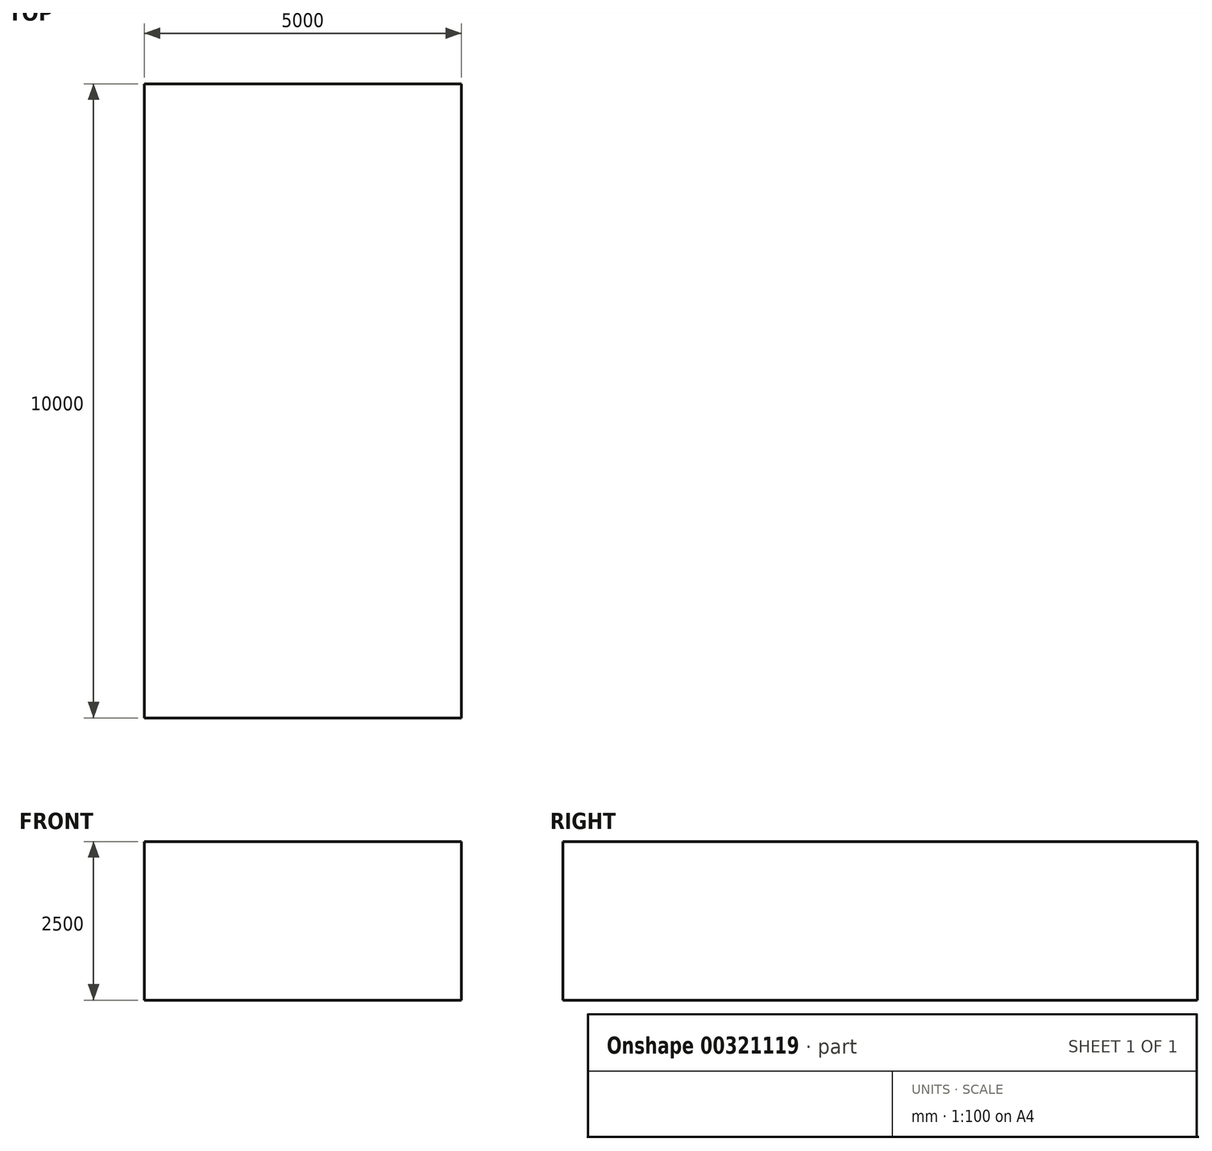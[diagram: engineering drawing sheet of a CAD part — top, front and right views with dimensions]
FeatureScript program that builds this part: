
annotation { "Feature Type Name" : "Feature", "Feature Type Description" : "" }
export const myFeature = defineFeature(function(context is Context, id is Id, definition is map)
    precondition{}
    {
        {
            var Q0;
            Q0=qCreatedBy(makeId("Front.planeOp"),FACE);
            var sketch = newSketch(context, id + "F0", { "sketchPlane" : qUnion([Q0])});
            skLineSegment(sketch, "E0.bottom", {"start": v(0, 0) * mm, "end": v(5000, 0) * mm});
            skLineSegment(sketch, "E0.top", {"start": v(0, -2500) * mm, "end": v(5000, -2500) * mm});
            skLineSegment(sketch, "E0.left", {"start": v(0, 0) * mm, "end": v(0, -2500) * mm});
            skLineSegment(sketch, "E0.right", {"start": v(5000, 0) * mm, "end": v(5000, -2500) * mm});
            skSolve(sketch);
        }
        {
            var Q0;
            Q0=makeQuery(id+"F0.imprint","IMPRINT",FACE,{"disambiguationData":[TD([[makeQuery(id+"F0.imprint","IMPRINT",EDGE,{"derivedFrom":sQuery(id+"F0.wireOp",EDGE,"E0.bottom")}),-1.0]])]});
            extrude(context, id + "F1", {"entities" : qUnion([Q0]), "depth" : 10000 * mm});
        }
    });
